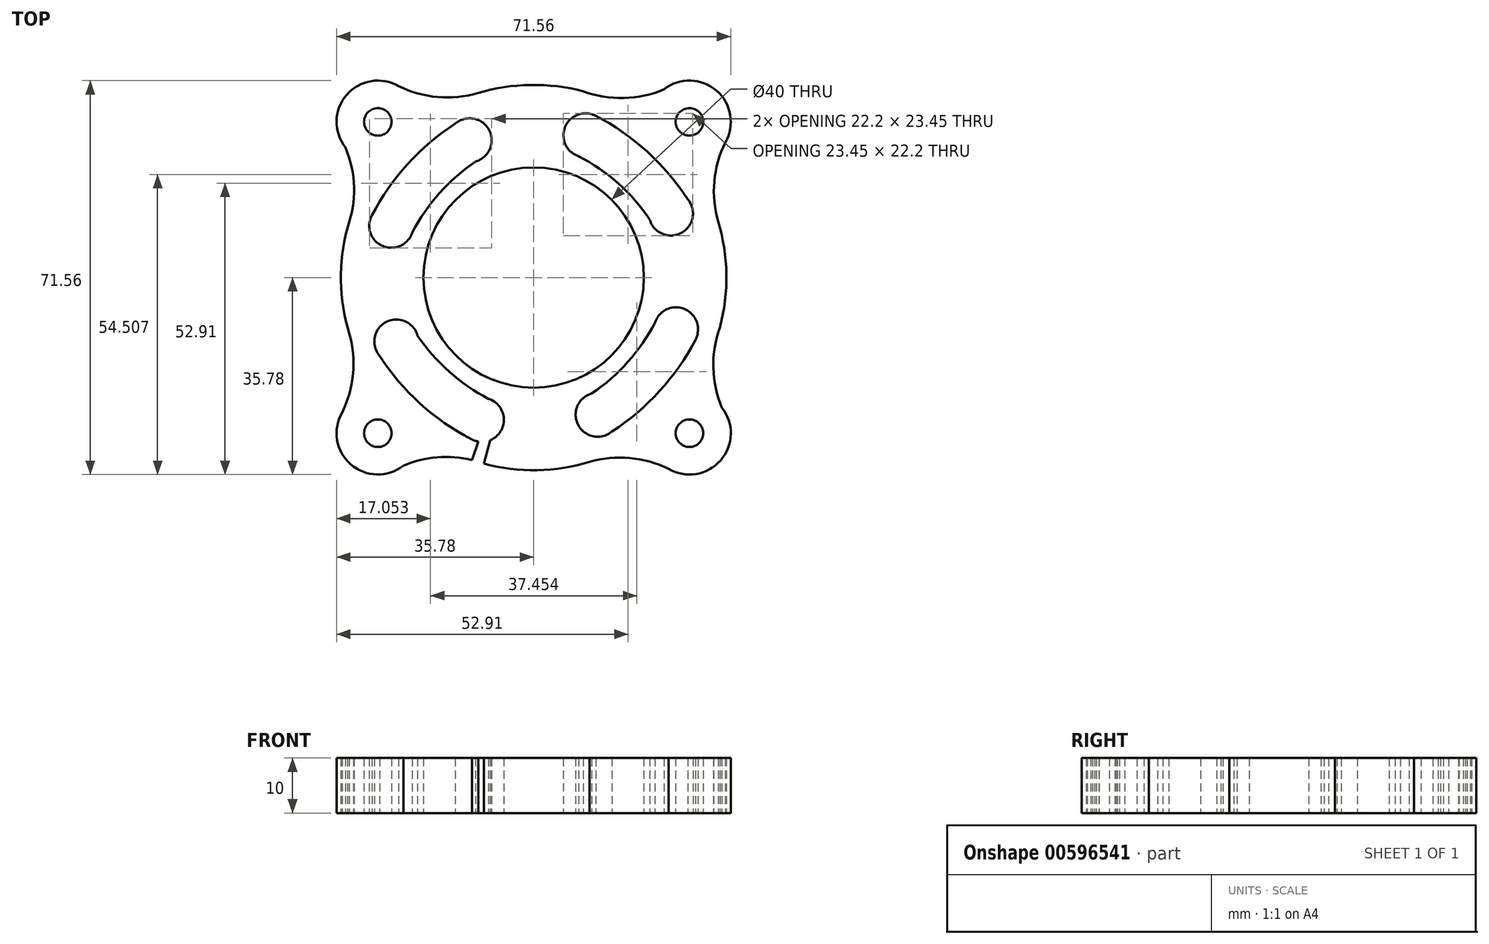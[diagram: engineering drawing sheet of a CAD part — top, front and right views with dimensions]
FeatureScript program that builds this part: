
annotation { "Feature Type Name" : "Feature", "Feature Type Description" : "" }
export const myFeature = defineFeature(function(context is Context, id is Id, definition is map)
    precondition{}
    {
        {
            var Q0;
            Q0=qCreatedBy(makeId("Top.planeOp"),FACE);
            var sketch = newSketch(context, id + "F0", { "sketchPlane" : qUnion([Q0])});
            skLineSegment(sketch, "E0.bottom", {"start": v(47.5, 47.5) * mm, "end": v(-47.5, 47.5) * mm});
            skLineSegment(sketch, "E0.top", {"start": v(47.5, -47.5) * mm, "end": v(-47.5, -47.5) * mm});
            skLineSegment(sketch, "E0.left", {"start": v(47.5, 47.5) * mm, "end": v(47.5, -47.5) * mm});
            skLineSegment(sketch, "E0.right", {"start": v(-47.5, 47.5) * mm, "end": v(-47.5, -47.5) * mm});
            skPoint(sketch, "E0.middle", {"position": v(0, 0) * mm});
            skArc(sketch, "E1", {"start": v(11.2, 33.16) * mm, "mid": v(0.54, 35) * mm, "end": v(-10.17, 33.5) * mm});
            skCircle(sketch, "E2", {"center": v(28.28, 28.28) * mm, "radius": 2.5 * mm});
            skArc(sketch, "E3", {"start": v(34.76, 24.5) * mm, "mid": v(33.2, 33.94) * mm, "end": v(23.65, 34.18) * mm});
            skCircle(sketch, "E4", {"center": v(0, 0) * mm, "radius": 20 * mm});
            skArc(sketch, "E5.1.0", {"start": v(-24.5, 34.76) * mm, "mid": v(-33.94, 33.2) * mm, "end": v(-34.18, 23.65) * mm});
            skCircle(sketch, "E5.1.1", {"center": v(-28.28, 28.28) * mm, "radius": 2.5 * mm});
            skArc(sketch, "E5.2.0", {"start": v(-34.76, -24.5) * mm, "mid": v(-33.2, -33.94) * mm, "end": v(-23.65, -34.18) * mm});
            skCircle(sketch, "E5.2.1", {"center": v(-28.28, -28.28) * mm, "radius": 2.5 * mm});
            skArc(sketch, "E5.3.0", {"start": v(24.5, -34.76) * mm, "mid": v(33.94, -33.2) * mm, "end": v(34.18, -23.65) * mm});
            skCircle(sketch, "E5.3.1", {"center": v(28.28, -28.28) * mm, "radius": 2.5 * mm});
            skLineSegment(sketch, "E6", {"start": v(28.28, 28.28) * mm, "end": v(0, 0) * mm});
            skArc(sketch, "E7", {"start": v(34.76, 24.5) * mm, "mid": v(32.8, 17.45) * mm, "end": v(33.5, 10.17) * mm});
            skArc(sketch, "E8", {"start": v(9.01, 33.82) * mm, "mid": v(16.36, 32.61) * mm, "end": v(23.65, 34.18) * mm});
            skArc(sketch, "E9.1.0", {"start": v(-33.82, 9.01) * mm, "mid": v(-32.61, 16.36) * mm, "end": v(-34.18, 23.65) * mm});
            skArc(sketch, "E9.1.1", {"start": v(-24.5, 34.76) * mm, "mid": v(-17.45, 32.8) * mm, "end": v(-10.17, 33.5) * mm});
            skArc(sketch, "E9.2.0", {"start": v(-9.01, -33.82) * mm, "mid": v(-16.36, -32.61) * mm, "end": v(-23.65, -34.18) * mm});
            skArc(sketch, "E9.2.1", {"start": v(-34.76, -24.5) * mm, "mid": v(-32.8, -17.45) * mm, "end": v(-33.5, -10.17) * mm});
            skArc(sketch, "E9.3.0", {"start": v(33.82, -9.01) * mm, "mid": v(32.61, -16.36) * mm, "end": v(34.18, -23.65) * mm});
            skArc(sketch, "E9.3.1", {"start": v(24.5, -34.76) * mm, "mid": v(17.45, -32.8) * mm, "end": v(10.17, -33.5) * mm});
            skLineSegment(sketch, "E10", {"start": v(0, 0) * mm, "end": v(-9.4, -25.84) * mm});
            skLineSegment(sketch, "E11", {"start": v(0, 47.5) * mm, "end": v(0, -47.5) * mm});
            skArc(sketch, "E12", {"start": v(-11.32, -29.36) * mm, "mid": v(-5.73, -27.41) * mm, "end": v(-8.18, -22.03) * mm});
            skArc(sketch, "E13.1.0", {"start": v(10.55, -21.07) * mm, "mid": v(8.1, -26.8) * mm, "end": v(14.22, -27.97) * mm});
            skArc(sketch, "E13.2.0", {"start": v(29.36, -11.32) * mm, "mid": v(27.41, -5.73) * mm, "end": v(22.03, -8.18) * mm});
            skArc(sketch, "E13.3.0", {"start": v(21.07, 10.55) * mm, "mid": v(26.8, 8.1) * mm, "end": v(27.97, 14.22) * mm});
            skArc(sketch, "E13.4.0", {"start": v(11.32, 29.36) * mm, "mid": v(5.73, 27.41) * mm, "end": v(8.18, 22.03) * mm});
            skArc(sketch, "E13.5.0", {"start": v(-10.55, 21.07) * mm, "mid": v(-8.1, 26.8) * mm, "end": v(-14.22, 27.97) * mm});
            skArc(sketch, "E13.6.0", {"start": v(-29.36, 11.32) * mm, "mid": v(-27.41, 5.73) * mm, "end": v(-22.03, 8.18) * mm});
            skArc(sketch, "E13.7.0", {"start": v(-21.07, -10.55) * mm, "mid": v(-26.8, -8.1) * mm, "end": v(-27.97, -14.22) * mm});
            skArc(sketch, "E14", {"start": v(13.24, -28.58) * mm, "mid": v(22.48, -21.05) * mm, "end": v(29.36, -11.32) * mm});
            skArc(sketch, "E15", {"start": v(10.55, -21.07) * mm, "mid": v(17.5, -14.9) * mm, "end": v(22.57, -7.1) * mm});
            skArc(sketch, "E16.1.0", {"start": v(28.58, 13.24) * mm, "mid": v(21.05, 22.48) * mm, "end": v(11.32, 29.36) * mm});
            skArc(sketch, "E16.1.1", {"start": v(21.07, 10.55) * mm, "mid": v(14.9, 17.5) * mm, "end": v(7.1, 22.57) * mm});
            skArc(sketch, "E16.2.0", {"start": v(-13.24, 28.58) * mm, "mid": v(-22.48, 21.05) * mm, "end": v(-29.36, 11.32) * mm});
            skArc(sketch, "E16.2.1", {"start": v(-10.55, 21.07) * mm, "mid": v(-17.5, 14.9) * mm, "end": v(-22.57, 7.1) * mm});
            skArc(sketch, "E16.3.0", {"start": v(-28.58, -13.24) * mm, "mid": v(-21.05, -22.48) * mm, "end": v(-11.32, -29.36) * mm});
            skArc(sketch, "E16.3.1", {"start": v(-21.07, -10.55) * mm, "mid": v(-14.9, -17.5) * mm, "end": v(-7.1, -22.57) * mm});
            skArc(sketch, "E17.trimOffspring", {"start": v(-33.16, 11.2) * mm, "mid": v(-35, 0.54) * mm, "end": v(-33.5, -10.17) * mm});
            skArc(sketch, "E18.trimOffspring", {"start": v(-11.2, -33.16) * mm, "mid": v(-0.54, -35) * mm, "end": v(10.17, -33.5) * mm});
            skArc(sketch, "E19.trimOffspring", {"start": v(33.16, -11.2) * mm, "mid": v(35, -0.54) * mm, "end": v(33.5, 10.17) * mm});
            skLineSegment(sketch, "E20", {"start": v(-11.2, -33.16) * mm, "end": v(0, 0) * mm});
            skLineSegment(sketch, "E21", {"start": v(-9.01, -33.82) * mm, "end": v(0, 0) * mm});
            skLineSegment(sketch, "E22", {"start": v(-23.65, -34.18) * mm, "end": v(0, 0) * mm});
            skSolve(sketch);
        }
        {
            var Q0;
            {var subQ30=sQuery(id+"F0.wireOp",EDGE,"E5.1.0");Q0=makeQuery(id+"F0.imprint","IMPRINT",FACE,{"disambiguationData":[TD([[makeQuery(id+"F0.imprint","IMPRINT",EDGE,{"derivedFrom":subQ30}),1.0]])]});}
            var Q1;
            Q1=makeQuery(id+"F0.imprint","IMPRINT",FACE,{"disambiguationData":[TD([[makeQuery(id+"F0.imprint","IMPRINT",EDGE,{"derivedFrom":sQuery(id+"F0.wireOp",EDGE,"E2")}),-1.0]])]});
            var Q2;
            {var subQ3=sQuery(id+"F0.wireOp",EDGE,"E22");var subQ7=sQuery(id+"F0.wireOp",EDGE,"E4");var subQ8=makeQuery(id+"F0.imprint","INTERSECT",VERTEX,{"derivedFrom":[subQ7,subQ3]});Q2=makeQuery(id+"F0.imprint","IMPRINT",FACE,{"disambiguationData":[TD([[makeQuery(id+"F0.imprint","IMPRINT",EDGE,{"disambiguationData":[TD([[subQ8,-1.0]])],"derivedFrom":subQ7}),-1.0]])]});}
            var Q3;
            {var subQ0=sQuery(id+"F0.wireOp",EDGE,"E21");var subQ8=sQuery(id+"F0.wireOp",EDGE,"E4");var subQ9=makeQuery(id+"F0.imprint","INTERSECT",VERTEX,{"derivedFrom":[subQ8,subQ0]});Q3=makeQuery(id+"F0.imprint","IMPRINT",FACE,{"disambiguationData":[TD([[makeQuery(id+"F0.imprint","IMPRINT",EDGE,{"disambiguationData":[TD([[subQ9,-1.0]])],"derivedFrom":subQ8}),-1.0]])]});}
            var Q4;
            {var subQ2=sQuery(id+"F0.wireOp",EDGE,"E20");var subQ4=sQuery(id+"F0.wireOp",EDGE,"E4");var subQ5=makeQuery(id+"F0.imprint","INTERSECT",VERTEX,{"derivedFrom":[subQ4,subQ2]});Q4=makeQuery(id+"F0.imprint","IMPRINT",FACE,{"disambiguationData":[TD([[makeQuery(id+"F0.imprint","IMPRINT",EDGE,{"disambiguationData":[TD([[subQ5,-1.0]])],"derivedFrom":subQ4}),-1.0]])]});}
            var Q5;
            {var subQ4=sQuery(id+"F0.wireOp",EDGE,"E20");var subQ6=sQuery(id+"F0.wireOp",EDGE,"E12");var subQ7=makeQuery(id+"F0.imprint","INTERSECT",VERTEX,{"disambiguationData":[OD(0.0)],"derivedFrom":[subQ6,subQ4]});Q5=makeQuery(id+"F0.imprint","IMPRINT",FACE,{"disambiguationData":[TD([[makeQuery(id+"F0.imprint","IMPRINT",EDGE,{"disambiguationData":[TD([[subQ7,-1.0]])],"derivedFrom":subQ6}),-1.0]])]});}
            var Q6;
            {var subQ0=sQuery(id+"F0.wireOp",EDGE,"E16.3.0");var subQ1=sQuery(id+"F0.wireOp",EDGE,"E12");var subQ2=makeQuery(id+"F0.imprint","INTERSECT",VERTEX,{"derivedFrom":[subQ1,subQ0]});Q6=makeQuery(id+"F0.imprint","IMPRINT",FACE,{"disambiguationData":[TD([[makeQuery(id+"F0.imprint","IMPRINT",EDGE,{"disambiguationData":[TD([[subQ2,-1.0]])],"derivedFrom":subQ1}),-1.0]])]});}
            var Q7;
            {var subQ0=sQuery(id+"F0.wireOp",EDGE,"E10");var subQ1=sQuery(id+"F0.wireOp",EDGE,"E4");var subQ2=makeQuery(id+"F0.imprint","INTERSECT",VERTEX,{"derivedFrom":[subQ1,subQ0]});Q7=makeQuery(id+"F0.imprint","IMPRINT",FACE,{"disambiguationData":[TD([[makeQuery(id+"F0.imprint","IMPRINT",EDGE,{"disambiguationData":[TD([[subQ2,-1.0]])],"derivedFrom":subQ1}),-1.0]])]});}
            extrude(context, id + "F1", {"entities" : qUnion([Q0, Q1, Q2, Q3, Q4, Q5, Q6, Q7]), "depth" : 10 * mm, "offsetDistance" : 25 * mm});
        }
    });
